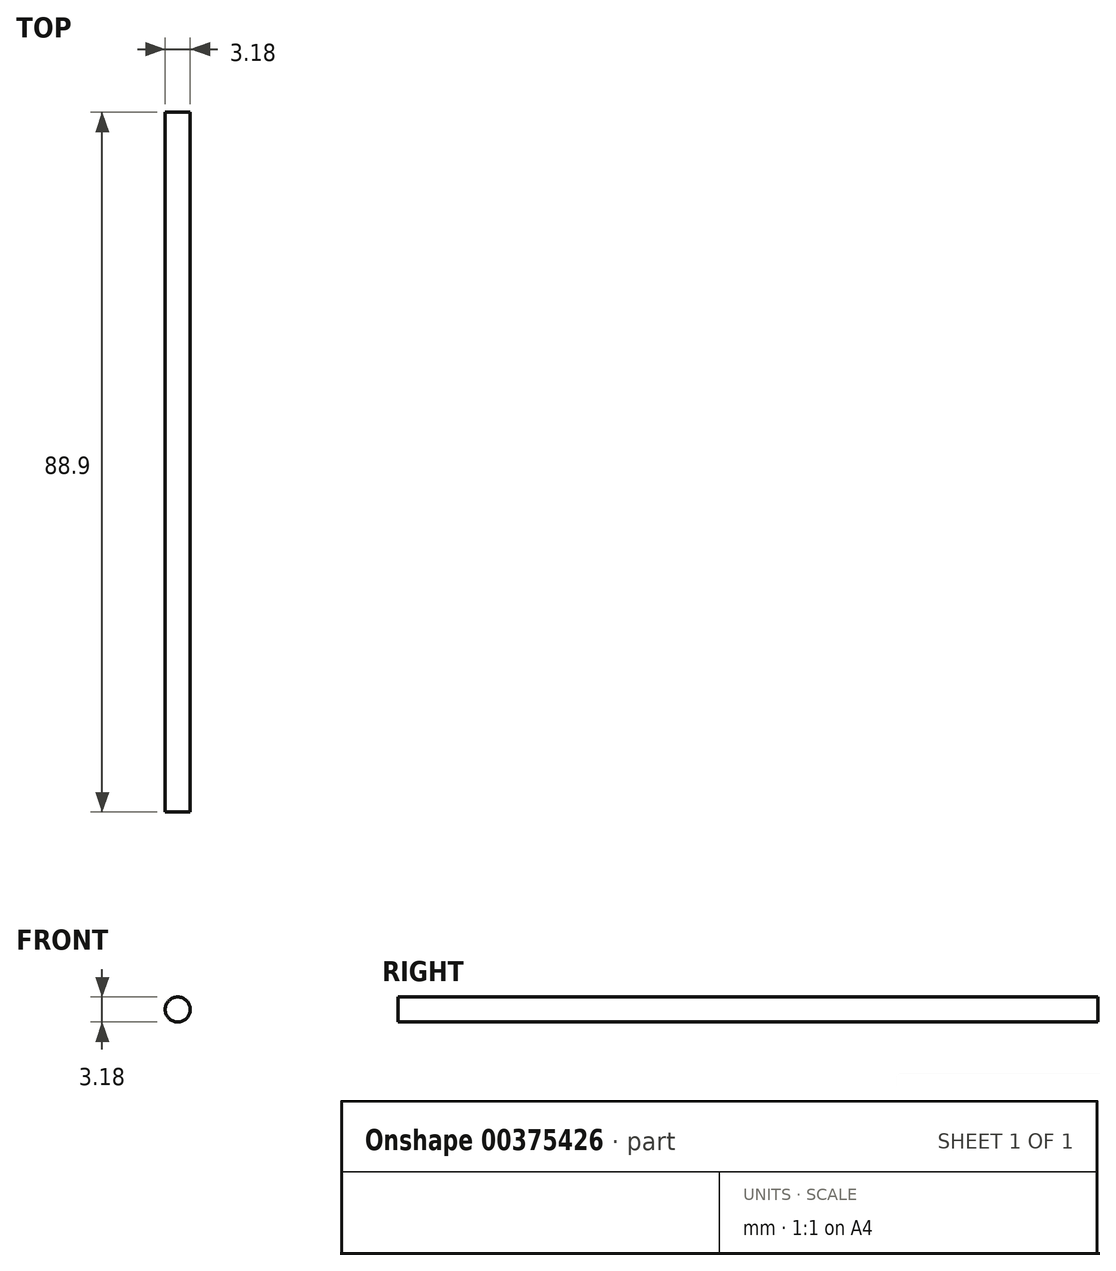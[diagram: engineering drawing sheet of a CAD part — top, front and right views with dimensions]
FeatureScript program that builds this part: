
annotation { "Feature Type Name" : "Feature", "Feature Type Description" : "" }
export const myFeature = defineFeature(function(context is Context, id is Id, definition is map)
    precondition{}
    {
        {
            var Q0;
            Q0=qCreatedBy(makeId("Front.planeOp"),FACE);
            var sketch = newSketch(context, id + "F0", { "sketchPlane" : qUnion([Q0])});
            skCircle(sketch, "E0", {"center": v(0, 0) * mm, "radius": 1.59 * mm});
            skSolve(sketch);
        }
        {
            var Q0;
            Q0=qSketchRegion(id+"F0",true);
            extrude(context, id + "F1", {"entities" : qUnion([Q0]), "depth" : 88.9 * mm, "symmetric" : true});
        }
    });
